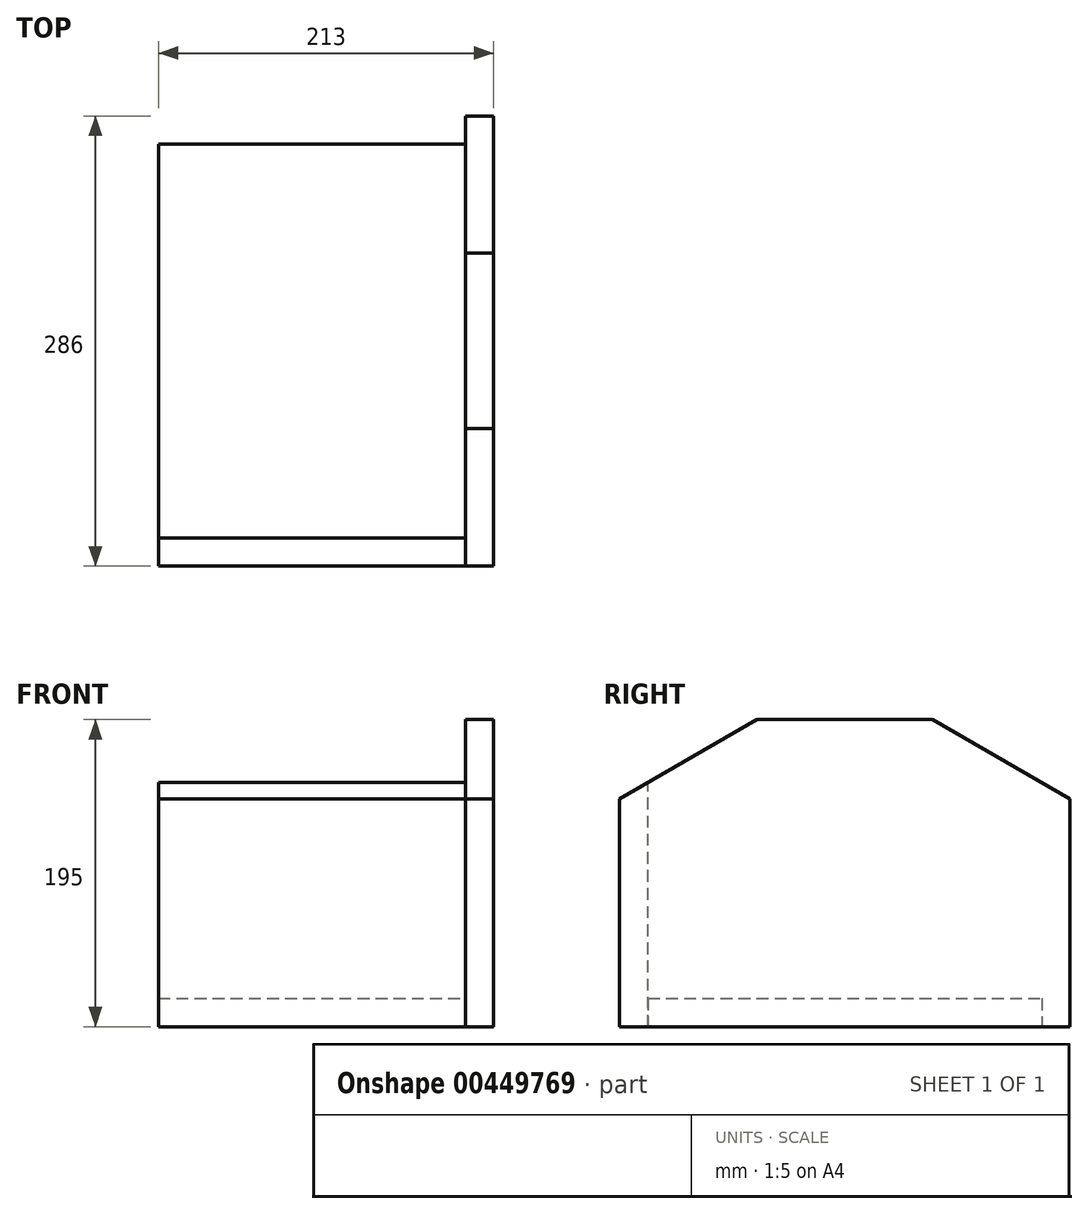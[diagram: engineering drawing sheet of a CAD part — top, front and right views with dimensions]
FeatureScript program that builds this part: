
annotation { "Feature Type Name" : "Feature", "Feature Type Description" : "" }
export const myFeature = defineFeature(function(context is Context, id is Id, definition is map)
    precondition{}
    {
        {
            var Q0;
            Q0=qCreatedBy(makeId("Front.planeOp"),FACE);
            var sketch = newSketch(context, id + "F0", { "sketchPlane" : qUnion([Q0])});
            skLineSegment(sketch, "E0.bottom", {"start": v(-97.5, 9) * mm, "end": v(97.5, 9) * mm});
            skLineSegment(sketch, "E0.top", {"start": v(-97.5, -9) * mm, "end": v(97.5, -9) * mm});
            skLineSegment(sketch, "E0.left", {"start": v(-97.5, 9) * mm, "end": v(-97.5, -9) * mm});
            skLineSegment(sketch, "E0.right", {"start": v(97.5, 9) * mm, "end": v(97.5, -9) * mm});
            skLineSegment(sketch, "E1", {"start": v(0, 0) * mm, "end": v(71.38, 0) * mm, "construction": true});
            skLineSegment(sketch, "E2", {"start": v(0, 0) * mm, "end": v(0, 40.66) * mm, "construction": true});
            skSolve(sketch);
        }
        {
            var Q0;
            Q0 = qSketchRegion(id + "F0", true);
            extrude(context, id + "F1", {"entities" : qUnion([Q0]), "endBound" : BoundingType.SYMMETRIC, "depth" : 250 * mm});
        }
        {
            var Q0;
            Q0=qCreatedBy(makeId("Front.planeOp"),FACE);
            cPlane(context, id + "F2", {"entities" : qUnion([Q0]), "cplaneType" : CPlaneType.OFFSET, "offset" : 250 / 2 * mm, "width" : 150 * mm, "height" : 150 * mm});
        }
        {
            var Q0;
            Q0=qCreatedBy(id+"F2.planeOp",FACE);
            var sketch = newSketch(context, id + "F3", { "sketchPlane" : qUnion([Q0])});
            skLineSegment(sketch, "E3", {"start": v(0, 0) * mm, "end": v(0, 172.38) * mm, "construction": true});
            skLineSegment(sketch, "E4.bottom", {"start": v(-97.5, -9) * mm, "end": v(97.5, -9) * mm});
            skLineSegment(sketch, "E4.top", {"start": v(-97.5, 146) * mm, "end": v(97.5, 146) * mm});
            skLineSegment(sketch, "E4.left", {"start": v(-97.5, -9) * mm, "end": v(-97.5, 146) * mm});
            skLineSegment(sketch, "E4.right", {"start": v(97.5, -9) * mm, "end": v(97.5, 146) * mm});
            skSolve(sketch);
        }
        {
            var Q0;
            Q0 = qSketchRegion(id + "F3", true);
            extrude(context, id + "F4", {"entities" : qUnion([Q0]), "depth" : 18 * mm});
        }
        {
            var Q0;
            Q0=qCreatedBy(makeId("Right.planeOp"),FACE);
            cPlane(context, id + "F5", {"entities" : qUnion([Q0]), "cplaneType" : CPlaneType.OFFSET, "offset" : (195 / 2) * mm, "width" : 150 * mm, "height" : 150 * mm});
        }
        {
            var Q0;
            Q0=makeQuery(id+"F4.opExtrude","SWEPT_FACE",FACE,{"disambiguationData":[OSD([sQuery(id+"F3.wireOp",EDGE,"E4.left")])]});
            var sketch = newSketch(context, id + "F6", { "sketchPlane" : qUnion([Q0])});
            skLineSegment(sketch, "E5", {"start": v(125, 146) * mm, "end": v(143, 135.6) * mm});
            skLineSegment(sketch, "E6", {"start": v(143, 146) * mm, "end": v(125, 146) * mm});
            skLineSegment(sketch, "E7", {"start": v(143, 146) * mm, "end": v(143, 135.6) * mm});
            skSolve(sketch);
        }
        {
            var Q0;
            Q0=makeQuery(id+"F6.imprint","IMPRINT",FACE,{"disambiguationData":[TD([[makeQuery(id+"F6.imprint","IMPRINT",EDGE,{"derivedFrom":sQuery(id+"F6.wireOp",EDGE,"E5")}),1.0]])]});
            extrude(context, id + "F7", {"entities" : qUnion([Q0]), "operationType" : NewBodyOperationType.REMOVE, "endBound" : BoundingType.THROUGH_ALL, "oppositeDirection" : true, "depth" : 25 * mm});
        }
        {
            var Q0;
            Q0=qCreatedBy(id+"F5.planeOp",FACE);
            var sketch = newSketch(context, id + "F8", { "sketchPlane" : qUnion([Q0])});
            skLineSegment(sketch, "E8.bottom", {"start": v(-143, 186) * mm, "end": v(143, 186) * mm});
            skLineSegment(sketch, "E8.top", {"start": v(-143, -9) * mm, "end": v(143, -9) * mm});
            skLineSegment(sketch, "E8.left", {"start": v(-143, 186) * mm, "end": v(-143, -9) * mm});
            skLineSegment(sketch, "E8.right", {"start": v(143, 186) * mm, "end": v(143, -9) * mm});
            skLineSegment(sketch, "E9", {"start": v(0, 0) * mm, "end": v(0, 164.11) * mm, "construction": true});
            skSolve(sketch);
        }
        {
            var Q0;
            Q0 = qSketchRegion(id + "F8", true);
            extrude(context, id + "F9", {"entities" : qUnion([Q0]), "depth" : 18 * mm});
        }
        {
            var Q0;
            Q0=makeQuery(id+"F9.opExtrude","CAP_FACE",FACE,{"disambiguationData":[OSD([sQuery(id+"F8.wireOp",EDGE,"E8.bottom"),sQuery(id+"F8.wireOp",EDGE,"E8.top"),sQuery(id+"F8.wireOp",EDGE,"E8.left"),sQuery(id+"F8.wireOp",EDGE,"E8.right")])],"isStart":false});
            var sketch = newSketch(context, id + "F10", { "sketchPlane" : qUnion([Q0])});
            skLineSegment(sketch, "E10", {"start": v(-143, 135.6) * mm, "end": v(-55.72, 186) * mm});
            skLineSegment(sketch, "E11", {"start": v(143, 135.6) * mm, "end": v(55.72, 186) * mm});
            skLineSegment(sketch, "E12", {"start": v(-143, 135.6) * mm, "end": v(-143, 186) * mm});
            skLineSegment(sketch, "E13", {"start": v(-143, 186) * mm, "end": v(-55.72, 186) * mm});
            skLineSegment(sketch, "E14", {"start": v(55.72, 186) * mm, "end": v(143, 186) * mm});
            skLineSegment(sketch, "E15", {"start": v(143, 186) * mm, "end": v(143, 135.6) * mm});
            skSolve(sketch);
        }
        {
            var Q0;
            Q0 = qSketchRegion(id + "F10", true);
            extrude(context, id + "F11", {"entities" : qUnion([Q0]), "operationType" : NewBodyOperationType.REMOVE, "endBound" : BoundingType.THROUGH_ALL, "oppositeDirection" : true, "depth" : 25 * mm});
        }
    });
